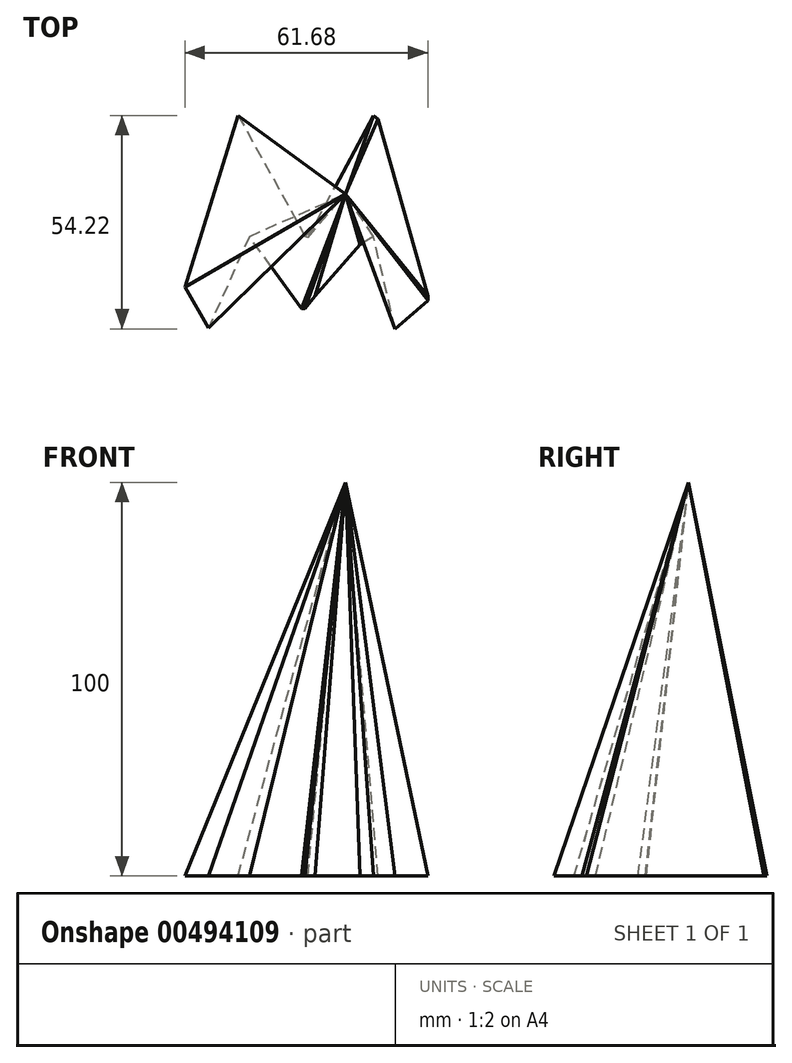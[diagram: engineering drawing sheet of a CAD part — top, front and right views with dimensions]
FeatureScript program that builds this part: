
annotation { "Feature Type Name" : "Feature", "Feature Type Description" : "" }
export const myFeature = defineFeature(function(context is Context, id is Id, definition is map)
    precondition{}
    {
        {
            var Q0;
            Q0=qCreatedBy(makeId("Top.planeOp"),FACE);
            var sketch = newSketch(context, id + "F0", { "sketchPlane" : qUnion([Q0])});
            skLineSegment(sketch, "E0", {"start": v(-40.74, -23.67) * mm, "end": v(-27.25, 19.94) * mm});
            skLineSegment(sketch, "E1", {"start": v(-27.25, 19.94) * mm, "end": v(-10.2, -10.76) * mm});
            skLineSegment(sketch, "E2", {"start": v(-9.54, -11.03) * mm, "end": v(7.17, 19.94) * mm});
            skLineSegment(sketch, "E3", {"start": v(8.32, 19.08) * mm, "end": v(20.94, -25.96) * mm});
            skLineSegment(sketch, "E4", {"start": v(20.94, -27.11) * mm, "end": v(12.62, -34.28) * mm});
            skLineSegment(sketch, "E5", {"start": v(12.62, -34.28) * mm, "end": v(7.17, -10.76) * mm});
            skLineSegment(sketch, "E6", {"start": v(3.7, -12.85) * mm, "end": v(-7.75, -25.96) * mm});
            skLineSegment(sketch, "E7", {"start": v(-7.75, -25.96) * mm, "end": v(-10.2, -29.11) * mm});
            skLineSegment(sketch, "E8", {"start": v(-11.19, -29.12) * mm, "end": v(-24.39, -10.76) * mm});
            skLineSegment(sketch, "E9", {"start": v(-24.39, -10.76) * mm, "end": v(-34.71, -34) * mm});
            skLineSegment(sketch, "E10", {"start": v(-40.74, -23.67) * mm, "end": v(-34.71, -34) * mm});
            skLineSegment(sketch, "E11", {"start": v(20.94, -27.11) * mm, "end": v(20.94, -25.96) * mm});
            skLineSegment(sketch, "E12", {"start": v(-11.19, -29.12) * mm, "end": v(-10.2, -29.11) * mm});
            skLineSegment(sketch, "E13", {"start": v(7.17, -10.76) * mm, "end": v(3.7, -12.85) * mm});
            skLineSegment(sketch, "E14", {"start": v(-9.54, -11.03) * mm, "end": v(-10.2, -10.76) * mm});
            skLineSegment(sketch, "E15", {"start": v(7.17, -10.76) * mm, "end": v(7.66, -12.85) * mm});
            skLineSegment(sketch, "E16", {"start": v(8.32, 19.08) * mm, "end": v(7.17, 19.94) * mm});
            skSolve(sketch);
        }
        {
            var Q0;
            Q0=qCreatedBy(makeId("Top.planeOp"),FACE);
            cPlane(context, id + "F1", {"entities" : qUnion([Q0]), "cplaneType" : CPlaneType.OFFSET, "offset" : 100 * mm, "width" : 150 * mm, "height" : 150 * mm});
        }
        {
            var Q0;
            Q0=qCreatedBy(id+"F1.planeOp",FACE);
            var sketch = newSketch(context, id + "F2", { "sketchPlane" : qUnion([Q0])});
            skPoint(sketch, "E17", {"position": v(0, 0) * mm});
            skSolve(sketch);
        }
        {
            var Q0;
            Q0 = qSketchRegion(id + "F0", true);
            var Q1;
            Q1=sQuery(id+"F2.wireOp",VERTEX,"E17");
            loft(context, id + "F3", {"sheetProfilesArray" : [{ "sheetProfileEntities" : qUnion([Q0]) }, { "sheetProfileEntities" : qUnion([Q1]) }]});
        }
    });
